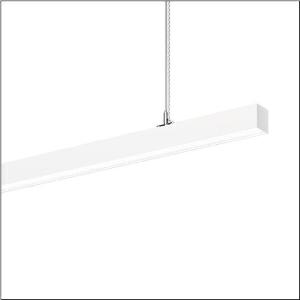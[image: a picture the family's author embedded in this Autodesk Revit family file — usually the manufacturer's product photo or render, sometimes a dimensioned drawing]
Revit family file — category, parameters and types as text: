
# Revit family: silica_r__21_51mx33da47wb_07b3
name_source: partatom
category: Lighting Fixtures
units: mm (PartAtom-declared; Revit-internal decimal feet)

## family parameters
Cut with Voids When Loaded = No
Host = Face
Light Source = No
Part Type = Normal
Room Calculation Point = No
Round Connector Dimension = Use Diameter
Shared = No

## types (1)
- --- (1 x LED, 5910 lm, 38.4 W, 4000K)
    Apparent Load = 38 VA
    CIE Flux Codes = 78 96 99 55 100
    Color Rendering = 80
    Color Temperature = 4000K
    Default Elevation = 1800 mm
    Description = Silica® 21, office luminaire, primary optical cover: prismatic diffuser, of PMMA, CAT 2 (L<= 3000cd/m²), light emission: direct/indirect distribution, primary light characteristic: symmetric, installation type: suspended mounting, LED, rated luminous flux: 5.910lm, luminous efficacy: 154lm/W, light colour: 840, colour temperature: 4000K, with terminal, 3+2-pole, max. 2.5mm², mains connection: 220..240V, AC, 50/60Hz, rated input power: 38.4W, luminaire housing, of aluminium, traffic white (RAL 9016), length: 1.204mm, width: 53mm, height: 53mm, protection rating (complete): IP20, insulation class (complete): insulation class I (protective earthing), certification: CE, permissible operating ambient temperature: 0..+35°C, standard: EN 50419, packaging unit: 1 piece
    Height = 53 mm
    Lamp = 1 x LED
    Lamp Light Flux = 5910 lm
    Lamp Power = 38.4 W
    Lamp count = 1
    Length = 1204 mm
    Luminous efficacy = 154 lm/W
    Manufacturer = Siteco
    ModVariant = No
    Model = 51MX33DA47WB
    Mounting Place = Ceiling
    Mounting Type = Pendant
    Number of Poles = 1
    OnlyDefault = Yes
    Power Factor = 1
    Product Name = Silica® 21
    Product group = office luminaire | ceiling pendant
    ProductGroupID = 902
    Protection Class = Protection class I
    Protection Degree = IP 20
    RLX_Detail_Level = 1
    RLX_Emergency_Light_Flux = 0 lm
    RLX_Emergency_Type = 0
    RLX_Emergency_Type_DB = No
    RlxData = <blob elided: 21205 chars, md5=1c6a2e13>
    Socket = socket
    Standby Power = 0 W
    System Light Flux = 5910 lm
    System Power = 38 W
    Type Comments = factory setting: luminous flux: 100 % | dim-lin: 254 | 323 mA
    Type Image = l_1335916.jpg
    URL = http://relux.com
    VarID = @adj_088087
    Voltage = 0 V
    Weight = 0.00 kg
    Width = 53 mm

## geometry (parser evidence)
native form markers: Blend x4, Sweep x13
no freeform markers — native parametric forms only
